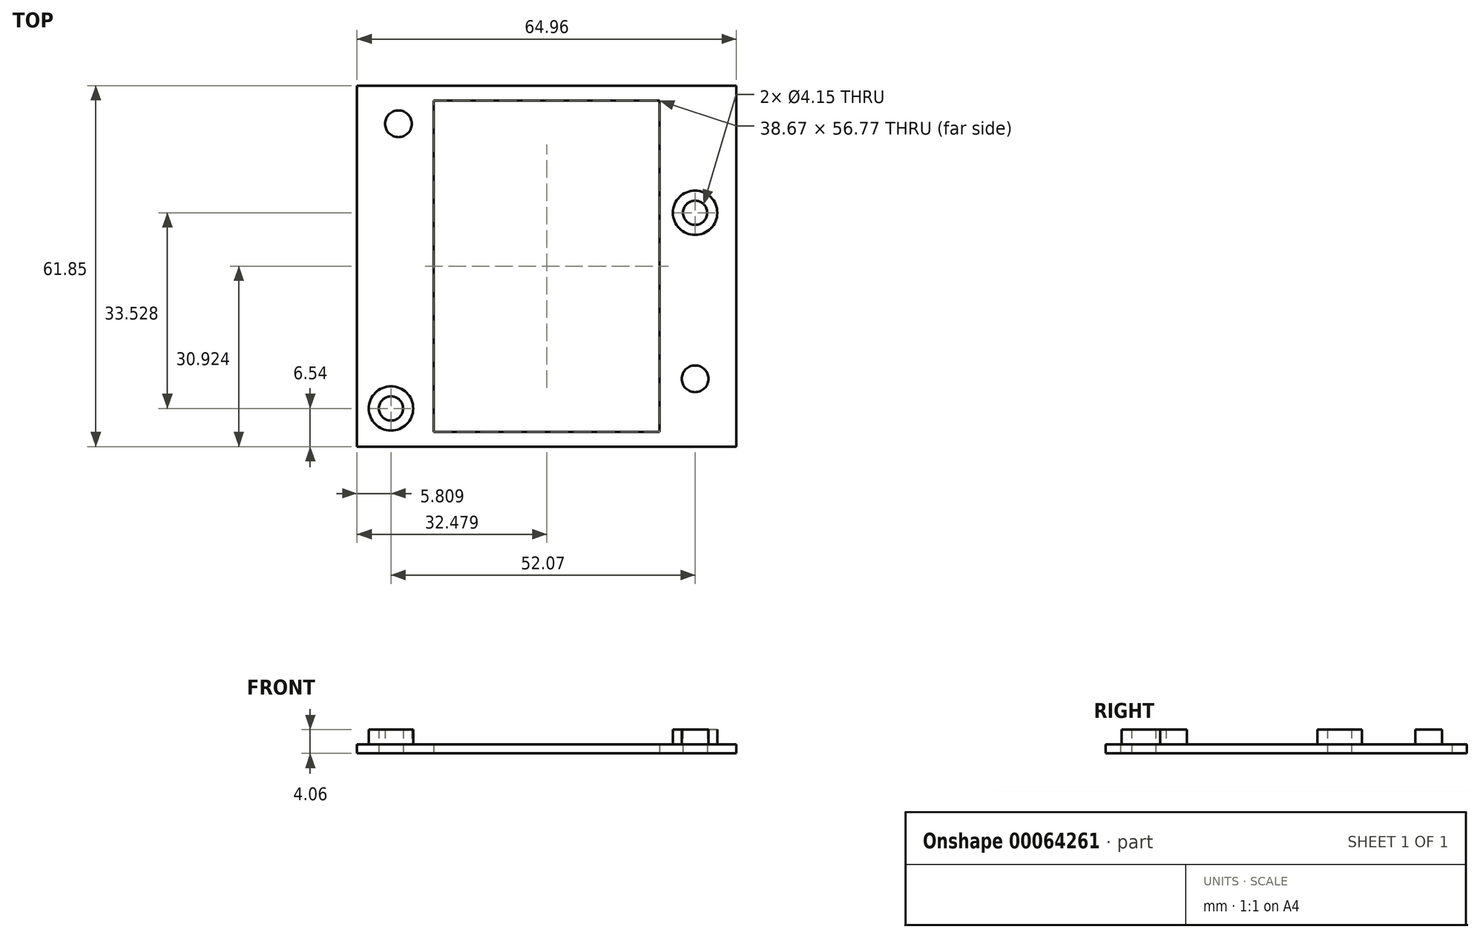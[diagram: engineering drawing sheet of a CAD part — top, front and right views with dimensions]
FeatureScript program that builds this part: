
annotation { "Feature Type Name" : "Feature", "Feature Type Description" : "" }
export const myFeature = defineFeature(function(context is Context, id is Id, definition is map)
    precondition{}
    {
        {
            var Q0;
            Q0=qCreatedBy(makeId("Top.planeOp"),FACE);
            var sketch = newSketch(context, id + "F0", { "sketchPlane" : qUnion([Q0])});
            skLineSegment(sketch, "E0.bottom", {"start": v(-98.88, 46.23) * mm, "end": v(3.23, 46.23) * mm});
            skLineSegment(sketch, "E0.top", {"start": v(-98.88, -7.62) * mm, "end": v(3.23, -7.62) * mm});
            skLineSegment(sketch, "E0.left", {"start": v(-98.88, 46.23) * mm, "end": v(-98.88, -7.62) * mm});
            skLineSegment(sketch, "E0.right", {"start": v(3.23, 46.23) * mm, "end": v(3.23, -7.62) * mm});
            skLineSegment(sketch, "E1.bottom", {"start": v(-91.26, 38.6) * mm, "end": v(-4.4, 38.6) * mm});
            skLineSegment(sketch, "E1.top", {"start": v(-91.26, 0) * mm, "end": v(-4.4, 0) * mm});
            skLineSegment(sketch, "E1.left", {"start": v(-91.26, 38.6) * mm, "end": v(-91.26, 0) * mm});
            skLineSegment(sketch, "E1.right", {"start": v(-4.4, 38.6) * mm, "end": v(-4.4, 0) * mm});
            skSolve(sketch);
        }
        {
            var Q0;
            Q0=qCreatedBy(makeId("Top.planeOp"),FACE);
            var sketch = newSketch(context, id + "F1", { "sketchPlane" : qUnion([Q0])});
            skCircle(sketch, "E2", {"center": v(-84.91, -5.08) * mm, "radius": 2.08 * mm});
            skCircle(sketch, "E3", {"center": v(-32.84, 0) * mm, "radius": 2.29 * mm});
            skCircle(sketch, "E4", {"center": v(-32.84, 28.45) * mm, "radius": 2.08 * mm});
            skCircle(sketch, "E5", {"center": v(-8.71, 43.69) * mm, "radius": 2.65 * mm});
            skCircle(sketch, "E6", {"center": v(-83.64, 43.69) * mm, "radius": 2.29 * mm});
            skCircle(sketch, "E7", {"center": v(-0.84, -5.08) * mm, "radius": 2.65 * mm});
            skLineSegment(sketch, "E8", {"start": v(-32.84, 46.23) * mm, "end": v(-32.84, -7.62) * mm, "construction": true});
            skLineSegment(sketch, "E9", {"start": v(-32.84, 28.45) * mm, "end": v(3.23, 28.45) * mm, "construction": true});
            skCircle(sketch, "E10", {"center": v(-8.71, 43.69) * mm, "radius": 3.8 * mm});
            skCircle(sketch, "E11", {"center": v(-32.84, 28.45) * mm, "radius": 3.8 * mm});
            skCircle(sketch, "E12", {"center": v(-84.91, -5.08) * mm, "radius": 3.8 * mm});
            skCircle(sketch, "E13", {"center": v(-0.84, -5.08) * mm, "radius": 3.8 * mm});
            skSolve(sketch);
        }
        {
            var Q0;
            Q0=qCreatedBy(makeId("Top.planeOp"),FACE);
            var sketch = newSketch(context, id + "F2", { "sketchPlane" : qUnion([Q0])});
            skCircle(sketch, "E14.cCircle", {"center": v(-83.64, 43.69) * mm, "radius": 3.5 * mm, "construction": true});
            skLineSegment(sketch, "E14.0", {"start": v(-79.6, 43.69) * mm, "end": v(-81.62, 40.2) * mm});
            skLineSegment(sketch, "E14.1", {"start": v(-81.62, 40.2) * mm, "end": v(-85.66, 40.2) * mm});
            skLineSegment(sketch, "E14.2", {"start": v(-85.66, 40.2) * mm, "end": v(-87.67, 43.69) * mm});
            skLineSegment(sketch, "E14.3", {"start": v(-87.67, 43.69) * mm, "end": v(-85.66, 47.18) * mm});
            skLineSegment(sketch, "E14.4", {"start": v(-85.66, 47.18) * mm, "end": v(-81.62, 47.18) * mm});
            skLineSegment(sketch, "E14.5", {"start": v(-81.62, 47.18) * mm, "end": v(-79.6, 43.69) * mm});
            skPoint(sketch, "E14.0.midPoint", {"position": v(-80.62, 41.94) * mm});
            skCircle(sketch, "E15.cCircle", {"center": v(-8.71, 43.69) * mm, "radius": 3.5 * mm, "construction": true});
            skLineSegment(sketch, "E15.0", {"start": v(-4.68, 43.69) * mm, "end": v(-6.7, 40.2) * mm});
            skLineSegment(sketch, "E15.1", {"start": v(-6.7, 40.2) * mm, "end": v(-10.73, 40.2) * mm});
            skLineSegment(sketch, "E15.2", {"start": v(-10.73, 40.2) * mm, "end": v(-12.74, 43.69) * mm});
            skLineSegment(sketch, "E15.3", {"start": v(-12.74, 43.69) * mm, "end": v(-10.73, 47.18) * mm});
            skLineSegment(sketch, "E15.4", {"start": v(-10.73, 47.18) * mm, "end": v(-6.7, 47.18) * mm});
            skLineSegment(sketch, "E15.5", {"start": v(-6.7, 47.18) * mm, "end": v(-4.68, 43.69) * mm});
            skPoint(sketch, "E15.0.midPoint", {"position": v(-5.69, 41.94) * mm});
            skCircle(sketch, "E16.cCircle", {"center": v(-32.84, 28.45) * mm, "radius": 3.5 * mm, "construction": true});
            skLineSegment(sketch, "E16.0", {"start": v(-28.8, 28.45) * mm, "end": v(-30.82, 24.96) * mm});
            skLineSegment(sketch, "E16.1", {"start": v(-30.82, 24.96) * mm, "end": v(-34.86, 24.96) * mm});
            skLineSegment(sketch, "E16.2", {"start": v(-34.86, 24.96) * mm, "end": v(-36.87, 28.45) * mm});
            skLineSegment(sketch, "E16.3", {"start": v(-36.87, 28.45) * mm, "end": v(-34.86, 31.94) * mm});
            skLineSegment(sketch, "E16.4", {"start": v(-34.86, 31.94) * mm, "end": v(-30.82, 31.94) * mm});
            skLineSegment(sketch, "E16.5", {"start": v(-30.82, 31.94) * mm, "end": v(-28.8, 28.45) * mm});
            skPoint(sketch, "E16.0.midPoint", {"position": v(-29.82, 26.7) * mm});
            skCircle(sketch, "E17.cCircle", {"center": v(-84.91, -5.08) * mm, "radius": 3.5 * mm, "construction": true});
            skLineSegment(sketch, "E17.0", {"start": v(-80.88, -5.08) * mm, "end": v(-82.9, -8.57) * mm});
            skLineSegment(sketch, "E17.1", {"start": v(-82.9, -8.57) * mm, "end": v(-86.93, -8.57) * mm});
            skLineSegment(sketch, "E17.2", {"start": v(-86.93, -8.57) * mm, "end": v(-88.94, -5.08) * mm});
            skLineSegment(sketch, "E17.3", {"start": v(-88.94, -5.08) * mm, "end": v(-86.93, -1.59) * mm});
            skLineSegment(sketch, "E17.4", {"start": v(-86.93, -1.59) * mm, "end": v(-82.9, -1.59) * mm});
            skLineSegment(sketch, "E17.5", {"start": v(-82.9, -1.59) * mm, "end": v(-80.88, -5.08) * mm});
            skPoint(sketch, "E17.0.midPoint", {"position": v(-81.89, -6.83) * mm});
            skCircle(sketch, "E18.cCircle", {"center": v(-32.84, 0) * mm, "radius": 3.5 * mm, "construction": true});
            skLineSegment(sketch, "E18.0", {"start": v(-28.8, 0) * mm, "end": v(-30.82, -3.5) * mm});
            skLineSegment(sketch, "E18.1", {"start": v(-30.82, -3.5) * mm, "end": v(-34.86, -3.5) * mm});
            skLineSegment(sketch, "E18.2", {"start": v(-34.86, -3.5) * mm, "end": v(-36.87, 0) * mm});
            skLineSegment(sketch, "E18.3", {"start": v(-36.87, 0) * mm, "end": v(-34.86, 3.5) * mm});
            skLineSegment(sketch, "E18.4", {"start": v(-34.86, 3.5) * mm, "end": v(-30.82, 3.5) * mm});
            skLineSegment(sketch, "E18.5", {"start": v(-30.82, 3.5) * mm, "end": v(-28.8, 0) * mm});
            skPoint(sketch, "E18.0.midPoint", {"position": v(-29.82, -1.75) * mm});
            skCircle(sketch, "E19.cCircle", {"center": v(-0.84, -5.08) * mm, "radius": 3.5 * mm, "construction": true});
            skLineSegment(sketch, "E19.0", {"start": v(3.2, -5.08) * mm, "end": v(1.18, -8.57) * mm});
            skLineSegment(sketch, "E19.1", {"start": v(1.18, -8.57) * mm, "end": v(-2.85, -8.57) * mm});
            skLineSegment(sketch, "E19.2", {"start": v(-2.85, -8.57) * mm, "end": v(-4.87, -5.08) * mm});
            skLineSegment(sketch, "E19.3", {"start": v(-4.87, -5.08) * mm, "end": v(-2.85, -1.59) * mm});
            skLineSegment(sketch, "E19.4", {"start": v(-2.85, -1.59) * mm, "end": v(1.18, -1.59) * mm});
            skLineSegment(sketch, "E19.5", {"start": v(1.18, -1.59) * mm, "end": v(3.2, -5.08) * mm});
            skPoint(sketch, "E19.0.midPoint", {"position": v(2.19, -6.83) * mm});
            skSolve(sketch);
        }
        {
            var Q0;
            Q0=qCreatedBy(makeId("Top.planeOp"),FACE);
            var sketch = newSketch(context, id + "F3", { "sketchPlane" : qUnion([Q0])});
            skCircle(sketch, "E20", {"center": v(-6.14, 28.58) * mm, "radius": 2.54 * mm});
            skCircle(sketch, "E21", {"center": v(-51.31, 29.3) * mm, "radius": 2.54 * mm});
            skCircle(sketch, "E22", {"center": v(-50.7, -1.38) * mm, "radius": 2.54 * mm});
            skCircle(sketch, "E23", {"center": v(-84.77, 15.99) * mm, "radius": 2.54 * mm});
            skSolve(sketch);
        }
        {
            var Q0;
            Q0=qCreatedBy(makeId("Top.planeOp"),FACE);
            var sketch = newSketch(context, id + "F4", { "sketchPlane" : qUnion([Q0])});
            skLineSegment(sketch, "E24.bottom", {"start": v(-90.72, 50.23) * mm, "end": v(-25.76, 50.23) * mm});
            skLineSegment(sketch, "E24.top", {"start": v(-90.72, -11.62) * mm, "end": v(-25.76, -11.62) * mm});
            skLineSegment(sketch, "E24.left", {"start": v(-90.72, 50.23) * mm, "end": v(-90.72, -11.62) * mm});
            skLineSegment(sketch, "E24.right", {"start": v(-25.76, 50.23) * mm, "end": v(-25.76, -11.62) * mm});
            skLineSegment(sketch, "E25.bottom", {"start": v(-77.58, 47.69) * mm, "end": v(-38.9, 47.69) * mm});
            skLineSegment(sketch, "E25.top", {"start": v(-77.58, -9.08) * mm, "end": v(-38.9, -9.08) * mm});
            skLineSegment(sketch, "E25.left", {"start": v(-77.58, 47.69) * mm, "end": v(-77.58, -9.08) * mm});
            skLineSegment(sketch, "E25.right", {"start": v(-38.9, 47.69) * mm, "end": v(-38.9, -9.08) * mm});
            skSolve(sketch);
        }
        {
            var Q0;
            Q0 = qSketchRegion(id + "F4", true);
            extrude(context, id + "F5", {"entities" : qUnion([Q0]), "depth" : 1.52 * mm, "offsetDistance" : 25.4 * mm});
        }
        {
            var Q0;
            Q0=makeQuery(id+"F1.imprint","IMPRINT",FACE,{"disambiguationData":[TD([[makeQuery(id+"F1.imprint","IMPRINT",EDGE,{"derivedFrom":sQuery(id+"F1.wireOp",EDGE,"E2")}),-1.0]])]});
            var Q1;
            Q1=makeQuery(id+"F1.imprint","IMPRINT",FACE,{"disambiguationData":[TD([[makeQuery(id+"F1.imprint","IMPRINT",EDGE,{"derivedFrom":sQuery(id+"F1.wireOp",EDGE,"E6")}),1.0]])]});
            var Q2;
            Q2=makeQuery(id+"F1.imprint","IMPRINT",FACE,{"disambiguationData":[TD([[makeQuery(id+"F1.imprint","IMPRINT",EDGE,{"derivedFrom":sQuery(id+"F1.wireOp",EDGE,"E3")}),1.0]])]});
            var Q3;
            Q3=makeQuery(id+"F1.imprint","IMPRINT",FACE,{"disambiguationData":[TD([[makeQuery(id+"F1.imprint","IMPRINT",EDGE,{"derivedFrom":sQuery(id+"F1.wireOp",EDGE,"E4")}),-1.0]])]});
            var Q4;
            Q4=sQuery(id+"F1.wireOp",EDGE,"E12");
            var Q5;
            Q5=sQuery(id+"F1.wireOp",EDGE,"E2");
            var Q6;
            Q6=sQuery(id+"F1.wireOp",EDGE,"E3");
            var Q7;
            Q7=sQuery(id+"F1.wireOp",EDGE,"E11");
            var Q8;
            Q8=sQuery(id+"F1.wireOp",EDGE,"E4");
            var Q9;
            Q9=sQuery(id+"F1.wireOp",EDGE,"E6");
            extrude(context, id + "F6", {"entities" : qUnion([Q0, Q1, Q2, Q3]), "operationType" : NewBodyOperationType.ADD, "surfaceEntities" : qUnion([Q4, Q5, Q6, Q7, Q8, Q9]), "depth" : 4.06 * mm, "offsetDistance" : 25.4 * mm});
        }
        {
            var Q0;
            Q0=makeQuery(id+"F1.imprint","IMPRINT",FACE,{"disambiguationData":[TD([[makeQuery(id+"F1.imprint","IMPRINT",EDGE,{"derivedFrom":sQuery(id+"F1.wireOp",EDGE,"E2")}),1.0]])]});
            var Q1;
            Q1=makeQuery(id+"F1.imprint","IMPRINT",FACE,{"disambiguationData":[TD([[makeQuery(id+"F1.imprint","IMPRINT",EDGE,{"derivedFrom":sQuery(id+"F1.wireOp",EDGE,"E4")}),1.0]])]});
            extrude(context, id + "F7", {"entities" : qUnion([Q0, Q1]), "operationType" : NewBodyOperationType.REMOVE, "depth" : 25.4 * mm, "offsetDistance" : 25.4 * mm});
        }
    });
